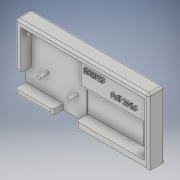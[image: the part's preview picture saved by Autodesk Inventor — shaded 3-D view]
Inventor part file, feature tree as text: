
AUTODESK INVENTOR PART (.ipt)
format: ipt  version: 2017 (Build 210142000, 142)  size: 584,192 bytes
history: native  units: in
note: dims shown in document units (in); Inventor stores cm internally (conversion verified against a paired STEP export)
features: sketch x11, extrude x10, fillet x4
ambient origin geometry x8: Origin, YZ Plane, XZ Plane, XY Plane, X Axis, Y Axis, Z Axis, Center Point
bodies: Solid1 (feature_tree)
feature tree (25):
  extrude  "Extrusion1"  Depth=2.4409in
  extrude  "Extrusion2"  Depth=0.5906in
  extrude  "Extrusion3"  Depth=0.3937in TaperAngle=0.0deg
  extrude  "Extrusion4"  Depth=0.0787in
  extrude  "Extrusion5"  Depth=0.3937in TaperAngle=0.0deg
  extrude  "Extrusion6"  Depth=0.5906in TaperAngle=0.0deg
  extrude  "Extrusion7"  Depth=1.9685in
  extrude  "Extrusion8"  Depth=0.1181in
  extrude  "Extrusion9"  Depth=0.1181in
  extrude  "Extrusion10"  Depth=0.3937in TaperAngle=0.0deg
  fillet  "Fillet1"  Radius=1.4567in
  fillet  "Fillet2"  Radius=0.3937in
  fillet  "Fillet3"  Radius=0.1181in
  fillet  "Fillet4"  Radius=0.0591in
  sketch  "Sketch15"  dims[d43=0.0787in d44=0.0787in d45=0.0787in d46=0.0787in]
  sketch  "Sketch3"  dims[d0=4.9213in d1=2.4409in]
  sketch  "Sketch4"  dims[d2=0.5906in d3=0.0in d4=2.0472in]
  sketch  "Sketch5"  dims[d5=2.0472in d7=0.3937in d8=0.0in]
  sketch  "Sketch6"  dims[d9=0.0787in d10=2.5197in]
  sketch  "Sketch7"  dims[d11=1.0433in d12=0.3937in d13=0.0in]
  sketch  "Sketch8"  dims[d14=0.4724in d15=0.5906in d16=0.0in]
  sketch  "Sketch9"  dims[d17=0.4331in d18=0.0in d19=1.9685in]
  sketch  "Sketch10"  dims[d20=1.9685in d28=0.1181in]
  sketch  "Sketch13"  dims[d29=0.1181in d30=0.1181in]
  sketch  "Sketch14"  dims[d31=0.315in d32=0.0in d34=0.3937in d35=0.0in d36=1.4567in d37=0.3937in d38=0.0in d39=0.1181in d40=0.0in d41=0.0591in d42=0.0in]
